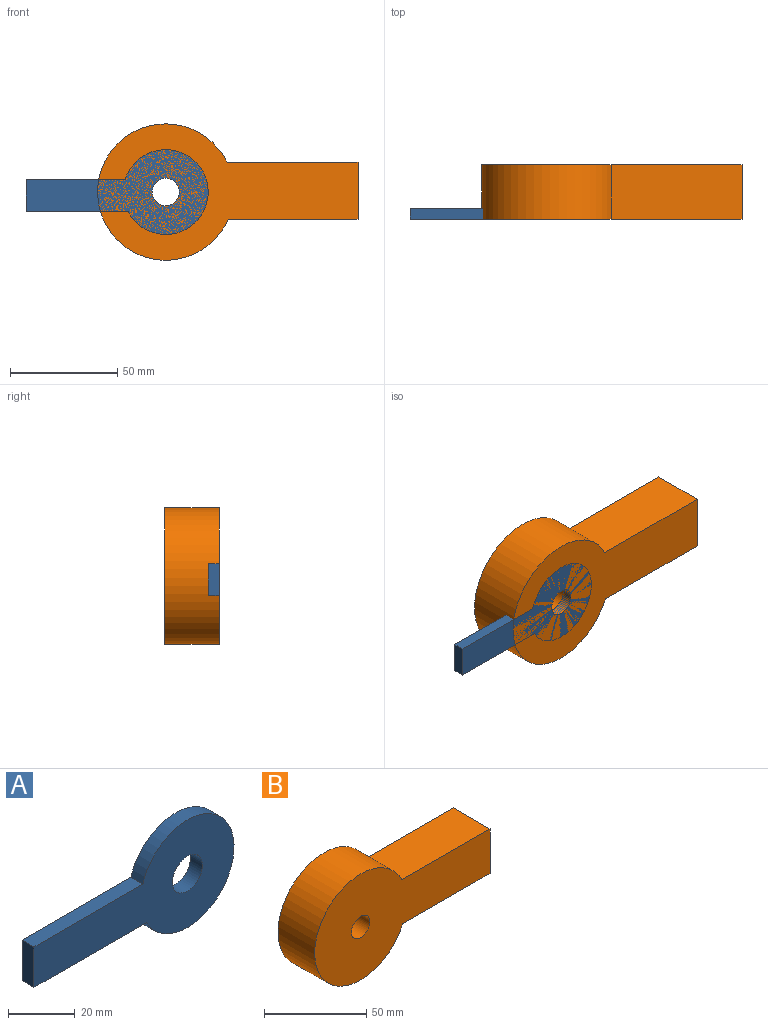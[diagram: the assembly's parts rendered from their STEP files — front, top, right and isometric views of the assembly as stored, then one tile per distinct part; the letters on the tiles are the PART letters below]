
ASSEMBLY  parts=2 mates=1
PART A: 7 faces, bbox 84.8x5.1x39.5 mm
  f0: plane 47.56x5.08mm, normal (0,0,-1), area 241.6mm2, adj f1,f3,f5,f6
  f1: cylinder r=19.76mm len=39.52mm, axis (0,1,0), area 553.1mm2, adj f0,f2,f5,f6
  f2: plane 46.1x5.08mm, normal (0,0,1), area 234.2mm2, adj f1,f3,f5,f6
  f3: plane 14.83x5.08mm, normal (-1,0,0), area 75.3mm2, adj f0,f2,f5,f6
  f4: cylinder r=6.35mm len=12.7mm, axis (0,1,0), area 202.7mm2, adj f5,f6
  f5: plane 84.8x39.52mm, normal (0,-1,0), area 1779.7mm2, adj f0,f1,f2,f3,f4
  f6: plane 84.8x39.52mm, normal (0,1,0), area 1779.7mm2, adj f0,f1,f2,f3,f4
PART B: 7 faces, bbox 121.3x25.4x63.5 mm
  f0: plane 60.99x25.4mm, normal (0,0,1), area 1549.2mm2, adj f1,f3,f5,f6
  f1: cylinder r=31.75mm len=63.5mm, axis (0,1,0), area 4369mm2, adj f0,f2,f5,f6
  f2: plane 60.39x25.4mm, normal (0,0,-1), area 1534mm2, adj f1,f3,f5,f6
  f3: plane 26.63x25.4mm, normal (1,0,0), area 676.3mm2, adj f0,f2,f5,f6
  f4: cylinder r=6.35mm len=25.4mm, axis (0,1,0), area 1013.4mm2, adj f5,f6
  f5: plane 121.26x63.5mm, normal (0,-1,0), area 4603.8mm2, adj f0,f1,f2,f3,f4
  f6: plane 121.26x63.5mm, normal (0,1,0), area 4603.8mm2, adj f0,f1,f2,f3,f4
PLACE A rot(axis=(0,1,0),0.2deg) t=(-102.93,-20.32,-6.22)mm
PLACE B t=(-102.93,0,-6.22)mm
MATE revolute A.f1 <-> B.f1  axis (0,-1,0) through (-102.93,-25.4,-6.22)mm
